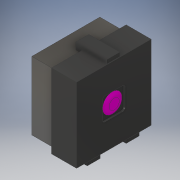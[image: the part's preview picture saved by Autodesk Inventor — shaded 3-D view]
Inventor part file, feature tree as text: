
AUTODESK INVENTOR PART (.ipt)
format: ipt  version: 2018 (Build 220112000, 112)  size: 171,008 bytes
history: native  units: in
note: dims shown in document units (in); Inventor stores cm internally (conversion verified against a paired STEP export)
features: extrude x5, sketch x5, fillet x2
ambient origin geometry x8: Origin, YZ Plane, XZ Plane, XY Plane, X Axis, Y Axis, Z Axis, Center Point
bodies: Solid1 (feature_tree), Solid2 (feature_tree)
feature tree (12):
  extrude  "Extrusion1"  Depth=0.4528in
  extrude  "Extrusion2"  Depth=0.4134in
  extrude  "Extrusion3"  Depth=0.1402in TaperAngle=0.0deg
  extrude  "Extrusion4"  Depth=0.0433in
  fillet  "Fillet1"  Radius=0.0787in
  extrude  "Extrusion5"  Depth=0.0492in
  fillet  "Fillet2"  Radius=0.5in
  sketch  "Sketch1"  dims[d0=0.4528in d1=0.4528in]
  sketch  "Sketch2"  dims[d2=0.1516in d3=0.0in d4=0.4134in]
  sketch  "Sketch3"  dims[d5=0.4134in d6=0.1402in d7=0.0in]
  sketch  "Sketch4"  dims[d8=0.0394in d9=0.0433in d10=0.0787in]
  sketch  "Sketch5"  dims[d11=0.0433in d12=0.0492in d13=0.5in d14=0.0394in d15=0.1476in d16=0.0in d17=0.0in d18=0.1378in d19=0.1378in d20=0.0098in d21=0.0in d22=0.0157in d23=0.1181in d24=0.0118in d25=0.0in d26=0.0394in]
